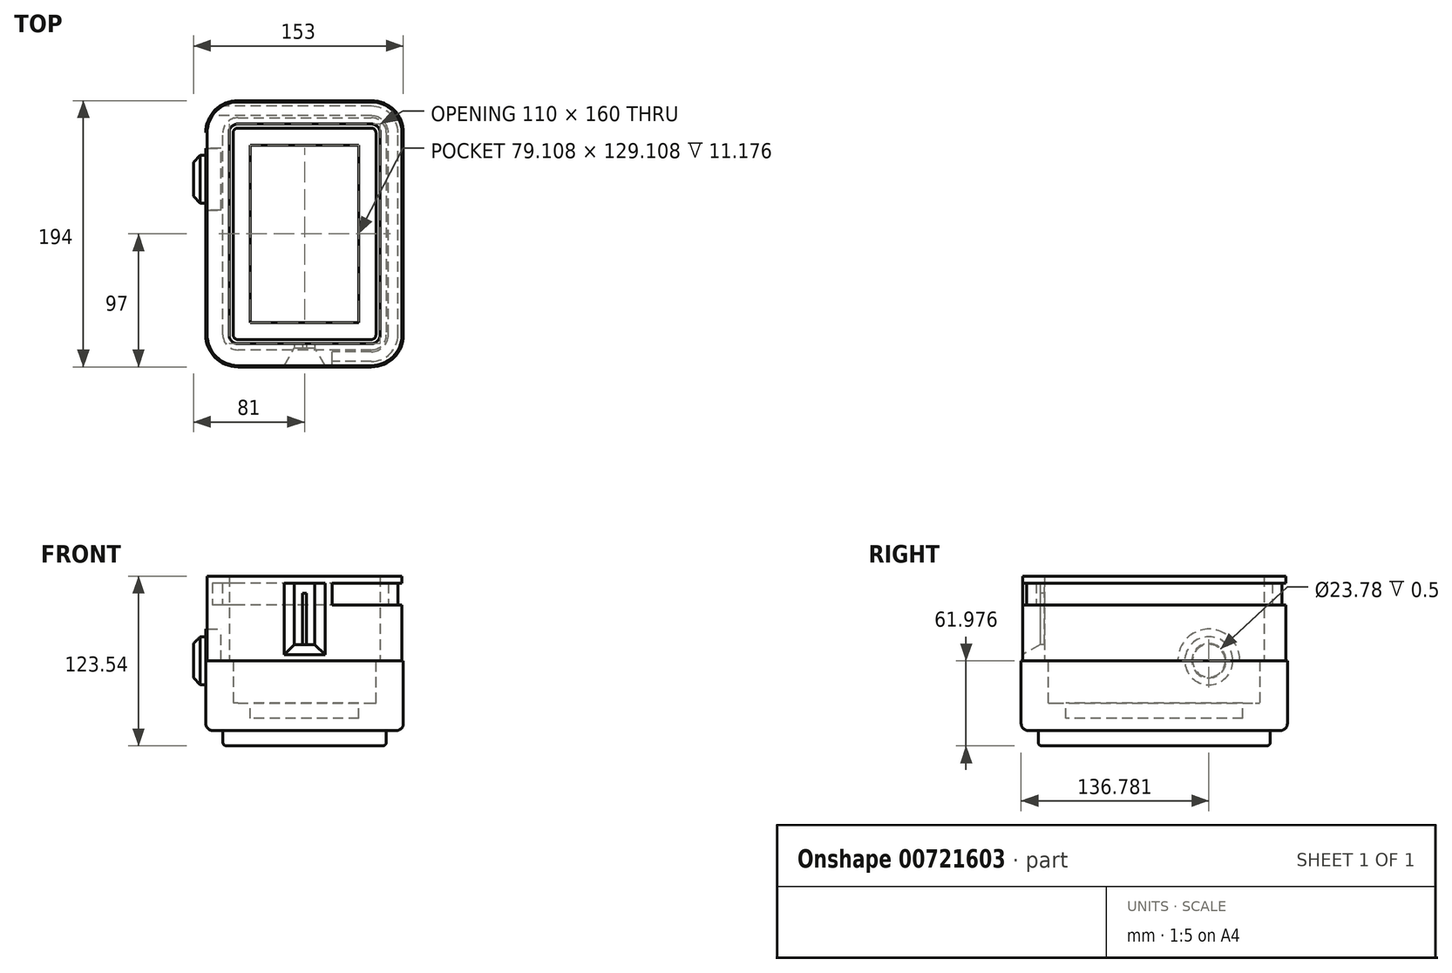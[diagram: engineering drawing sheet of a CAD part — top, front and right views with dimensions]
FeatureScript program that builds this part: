
annotation { "Feature Type Name" : "Feature", "Feature Type Description" : "" }
export const myFeature = defineFeature(function(context is Context, id is Id, definition is map)
    precondition{}
    {
        {
            var Q0;
            Q0=qCreatedBy(makeId("Top.planeOp"),FACE);
            var sketch = newSketch(context, id + "F0", { "sketchPlane" : qUnion([Q0])});
            skLineSegment(sketch, "E0.bottom", {"start": v(-21.35, -6.35) * mm, "end": v(-118.65, -6.35) * mm});
            skLineSegment(sketch, "E0.top", {"start": v(-21.35, 153.65) * mm, "end": v(-118.65, 153.65) * mm});
            skLineSegment(sketch, "E0.left", {"start": v(-15, 0) * mm, "end": v(-15, 147.3) * mm});
            skLineSegment(sketch, "E0.right", {"start": v(-125, 0) * mm, "end": v(-125, 147.3) * mm});
            skPoint(sketch, "E1.visualSharp", {"position": v(-125, 153.65) * mm});
            skArc(sketch, "E1.filletArc", {"start": v(-118.65, 153.65) * mm, "mid": v(-123.14, 151.8) * mm, "end": v(-125, 147.3) * mm});
            skPoint(sketch, "E2.visualSharp", {"position": v(-15, 153.65) * mm});
            skArc(sketch, "E2.filletArc", {"start": v(-15, 147.3) * mm, "mid": v(-16.86, 151.8) * mm, "end": v(-21.35, 153.65) * mm});
            skPoint(sketch, "E3.visualSharp", {"position": v(-15, -6.35) * mm});
            skArc(sketch, "E3.filletArc", {"start": v(-21.35, -6.35) * mm, "mid": v(-16.86, -4.5) * mm, "end": v(-15, 0) * mm});
            skPoint(sketch, "E4.visualSharp", {"position": v(-125, -6.35) * mm});
            skArc(sketch, "E4.filletArc", {"start": v(-125, 0) * mm, "mid": v(-123.14, -4.5) * mm, "end": v(-118.65, -6.35) * mm});
            skArc(sketch, "E5.0", {"start": v(-140, 0) * mm, "mid": v(-133.75, -15.1) * mm, "end": v(-118.65, -21.35) * mm});
            skLineSegment(sketch, "E5.1", {"start": v(-21.35, -21.35) * mm, "end": v(-118.65, -21.35) * mm});
            skLineSegment(sketch, "E5.2", {"start": v(-140, 0) * mm, "end": v(-140, 147.3) * mm});
            skArc(sketch, "E5.3", {"start": v(-21.35, -21.35) * mm, "mid": v(-6.25, -15.1) * mm, "end": v(0, 0) * mm});
            skArc(sketch, "E5.4", {"start": v(-118.65, 168.65) * mm, "mid": v(-133.75, 162.4) * mm, "end": v(-140, 147.3) * mm});
            skLineSegment(sketch, "E5.5", {"start": v(-21.35, 168.65) * mm, "end": v(-118.65, 168.65) * mm});
            skArc(sketch, "E5.6", {"start": v(0, 147.3) * mm, "mid": v(-6.25, 162.4) * mm, "end": v(-21.35, 168.65) * mm});
            skLineSegment(sketch, "E5.7", {"start": v(0, 0) * mm, "end": v(0, 147.3) * mm});
            skPoint(sketch, "E6.visualSharp", {"position": v(-322.23, 56.74) * mm});
            skPoint(sketch, "E7.visualSharp", {"position": v(-212.23, 56.74) * mm});
            skPoint(sketch, "E8.visualSharp", {"position": v(-212.23, -103.26) * mm});
            skPoint(sketch, "E9.visualSharp", {"position": v(-322.23, -103.26) * mm});
            skLineSegment(sketch, "E10.0", {"start": v(-21.35, 169.65) * mm, "end": v(-118.65, 169.65) * mm});
            skArc(sketch, "E10.1", {"start": v(1, 147.3) * mm, "mid": v(-5.55, 163.1) * mm, "end": v(-21.35, 169.65) * mm});
            skArc(sketch, "E10.2", {"start": v(-118.65, 169.65) * mm, "mid": v(-134.45, 163.1) * mm, "end": v(-141, 147.3) * mm});
            skLineSegment(sketch, "E10.3", {"start": v(1, 0) * mm, "end": v(1, 147.3) * mm});
            skLineSegment(sketch, "E10.4", {"start": v(-141, 0) * mm, "end": v(-141, 147.3) * mm});
            skArc(sketch, "E10.5", {"start": v(-141, 0) * mm, "mid": v(-134.45, -15.8) * mm, "end": v(-118.65, -22.35) * mm});
            skLineSegment(sketch, "E10.6", {"start": v(-21.35, -22.35) * mm, "end": v(-118.65, -22.35) * mm});
            skArc(sketch, "E10.7", {"start": v(-21.35, -22.35) * mm, "mid": v(-5.55, -15.8) * mm, "end": v(1, 0) * mm});
            skSolve(sketch);
        }
        {
            var Q0;
            Q0=makeQuery(id+"F0.imprint","IMPRINT",FACE,{"disambiguationData":[TD([[makeQuery(id+"F0.imprint","IMPRINT",EDGE,{"derivedFrom":sQuery(id+"F0.wireOp",EDGE,"E0.bottom")}),1.0]])]});
            var Q1;
            Q1=makeQuery(id+"F0.imprint","IMPRINT",FACE,{"disambiguationData":[TD([[makeQuery(id+"F0.imprint","IMPRINT",EDGE,{"derivedFrom":sQuery(id+"F0.wireOp",EDGE,"E5.0")}),-1.0]])]});
            extrude(context, id + "F1", {"entities" : qUnion([Q0, Q1]), "depth" : 100 * mm, "offsetDistance" : 25.4 * mm});
        }
        {
            var Q0;
            Q0=makeQuery(id+"F1.opExtrude","CAP_FACE",FACE,{"disambiguationData":[OSD([sQuery(id+"F0.wireOp",EDGE,"E0.bottom"),sQuery(id+"F0.wireOp",EDGE,"E0.top"),sQuery(id+"F0.wireOp",EDGE,"E0.left"),sQuery(id+"F0.wireOp",EDGE,"E0.right"),sQuery(id+"F0.wireOp",EDGE,"E1.filletArc"),sQuery(id+"F0.wireOp",EDGE,"E2.filletArc"),sQuery(id+"F0.wireOp",EDGE,"E3.filletArc"),sQuery(id+"F0.wireOp",EDGE,"E4.filletArc"),sQuery(id+"F0.wireOp",EDGE,"E10.0"),sQuery(id+"F0.wireOp",EDGE,"E10.1"),sQuery(id+"F0.wireOp",EDGE,"E10.2"),sQuery(id+"F0.wireOp",EDGE,"E10.3"),sQuery(id+"F0.wireOp",EDGE,"E10.4"),sQuery(id+"F0.wireOp",EDGE,"E10.5"),sQuery(id+"F0.wireOp",EDGE,"E10.6"),sQuery(id+"F0.wireOp",EDGE,"E10.7")])],"isStart":false});
            var sketch = newSketch(context, id + "F2", { "sketchPlane" : qUnion([Q0])});
            skArc(sketch, "E11.0", {"start": v(-9, 147.3) * mm, "mid": v(-12.62, 156.03) * mm, "end": v(-21.35, 159.65) * mm});
            skLineSegment(sketch, "E11.1", {"start": v(-9, 0) * mm, "end": v(-9, 147.3) * mm});
            skLineSegment(sketch, "E11.2", {"start": v(-21.35, 159.65) * mm, "end": v(-118.65, 159.65) * mm});
            skArc(sketch, "E11.3", {"start": v(-21.35, -12.35) * mm, "mid": v(-12.62, -8.73) * mm, "end": v(-9, 0) * mm});
            skArc(sketch, "E11.4", {"start": v(-118.65, 159.65) * mm, "mid": v(-127.38, 156.03) * mm, "end": v(-131, 147.3) * mm});
            skLineSegment(sketch, "E11.5", {"start": v(-131, 0) * mm, "end": v(-131, 147.3) * mm});
            skArc(sketch, "E11.6", {"start": v(-131, 0) * mm, "mid": v(-127.38, -8.73) * mm, "end": v(-118.65, -12.35) * mm});
            skLineSegment(sketch, "E11.7", {"start": v(-21.35, -12.35) * mm, "end": v(-118.65, -12.35) * mm});
            skLineSegment(sketch, "E12", {"start": v(-118.65, 159.65) * mm, "end": v(-137.28, 159.65) * mm});
            skLineSegment(sketch, "E13", {"start": v(-50, -22.35) * mm, "end": v(-50, -12.35) * mm});
            skPoint(sketch, "E14", {"position": v(-70, -12.35) * mm});
            skSolve(sketch);
        }
        {
            var Q0;
            Q0=makeQuery(id+"F2.imprint","IMPRINT",FACE,{"disambiguationData":[TD([[makeQuery(id+"F2.imprint","IMPRINT",EDGE,{"derivedFrom":sQuery(id+"F2.wireOp",EDGE,"E11.4")}),-1.0]])]});
            var Q1;
            Q1=makeQuery(id+"F2.imprint","IMPRINT",FACE,{"disambiguationData":[TD([[makeQuery(id+"F2.imprint","IMPRINT",EDGE,{"derivedFrom":sQuery(id+"F2.wireOp",EDGE,"E11.0")}),1.0]])]});
            extrude(context, id + "F3", {"entities" : qUnion([Q0, Q1]), "operationType" : NewBodyOperationType.ADD, "depth" : 16 * mm, "offsetDistance" : 25.4 * mm});
        }
        {
            var Q0;
            Q0=makeQuery(id+"F3.opExtrude","CAP_FACE",FACE,{"disambiguationData":[OSD([sQuery(id+"F0.wireOp",EDGE,"E0.bottom"),sQuery(id+"F0.wireOp",EDGE,"E0.top"),sQuery(id+"F0.wireOp",EDGE,"E0.left"),sQuery(id+"F0.wireOp",EDGE,"E0.right"),sQuery(id+"F0.wireOp",EDGE,"E1.filletArc"),sQuery(id+"F0.wireOp",EDGE,"E2.filletArc"),sQuery(id+"F0.wireOp",EDGE,"E3.filletArc"),sQuery(id+"F0.wireOp",EDGE,"E4.filletArc"),sQuery(id+"F0.wireOp",EDGE,"E10.2"),sQuery(id+"F0.wireOp",EDGE,"E10.4"),sQuery(id+"F0.wireOp",EDGE,"E10.5"),sQuery(id+"F0.wireOp",EDGE,"E10.6"),sQuery(id+"F2.wireOp",EDGE,"E11.0"),sQuery(id+"F2.wireOp",EDGE,"E11.1"),sQuery(id+"F2.wireOp",EDGE,"E11.2"),sQuery(id+"F2.wireOp",EDGE,"E11.3"),sQuery(id+"F2.wireOp",EDGE,"E11.7"),sQuery(id+"F2.wireOp",EDGE,"E12"),sQuery(id+"F2.wireOp",EDGE,"E13")])],"isStart":false});
            var sketch = newSketch(context, id + "F4", { "sketchPlane" : qUnion([Q0])});
            skSolve(sketch);
        }
        {
            var Q0;
            Q0=makeQuery(id+"F4.imprint","IMPRINT",FACE,{"disambiguationData":[TD([[makeQuery(id+"F4.imprint","IMPRINT",EDGE,{"derivedFrom":makeQuery(id+"F3.opExtrude","CAP_EDGE",EDGE,{"disambiguationData":[OSD([sQuery(id+"F2.wireOp",EDGE,"E11.0")])],"isStart":false})}),1.0]])]});
            var sketch = newSketch(context, id + "F5", { "sketchPlane" : qUnion([Q0])});
            skArc(sketch, "E15.0", {"start": v(-141, 0) * mm, "mid": v(-134.45, -15.8) * mm, "end": v(-118.65, -22.35) * mm});
            skLineSegment(sketch, "E15.1", {"start": v(-21.35, -22.35) * mm, "end": v(-118.65, -22.35) * mm});
            skLineSegment(sketch, "E15.2", {"start": v(-141, 0) * mm, "end": v(-141, 147.3) * mm});
            skArc(sketch, "E15.3", {"start": v(-21.35, -22.35) * mm, "mid": v(-5.55, -15.8) * mm, "end": v(1, 0) * mm});
            skArc(sketch, "E15.4", {"start": v(-118.65, 169.65) * mm, "mid": v(-134.45, 163.1) * mm, "end": v(-141, 147.3) * mm});
            skLineSegment(sketch, "E15.5", {"start": v(-21.35, 169.65) * mm, "end": v(-118.65, 169.65) * mm});
            skArc(sketch, "E15.6", {"start": v(1, 147.3) * mm, "mid": v(-5.55, 163.1) * mm, "end": v(-21.35, 169.65) * mm});
            skLineSegment(sketch, "E15.7", {"start": v(1, 0) * mm, "end": v(1, 147.3) * mm});
            skSolve(sketch);
        }
        {
            var Q0;
            Q0=makeQuery(id+"F4.imprint","IMPRINT",FACE,{"disambiguationData":[TD([[makeQuery(id+"F4.imprint","IMPRINT",EDGE,{"derivedFrom":makeQuery(id+"F3.opExtrude","CAP_EDGE",EDGE,{"disambiguationData":[OSD([sQuery(id+"F2.wireOp",EDGE,"E11.0")])],"isStart":false})}),1.0]])]});
            var Q1;
            {var subQ3=sQuery(id+"F5.wireOp",EDGE,"E15.3");Q1=makeQuery(id+"F5.imprint","IMPRINT",FACE,{"disambiguationData":[TD([[makeQuery(id+"F5.imprint","IMPRINT",EDGE,{"derivedFrom":subQ3}),1.0]])]});}
            extrude(context, id + "F6", {"entities" : qUnion([Q0, Q1]), "operationType" : NewBodyOperationType.ADD, "depth" : 5 * mm, "offsetDistance" : 25.4 * mm});
        }
        {
            var Q0;
            Q0=makeQuery(id+"F1.opExtrude","CAP_FACE",FACE,{"disambiguationData":[OSD([sQuery(id+"F0.wireOp",EDGE,"E0.bottom"),sQuery(id+"F0.wireOp",EDGE,"E0.top"),sQuery(id+"F0.wireOp",EDGE,"E0.left"),sQuery(id+"F0.wireOp",EDGE,"E0.right"),sQuery(id+"F0.wireOp",EDGE,"E1.filletArc"),sQuery(id+"F0.wireOp",EDGE,"E2.filletArc"),sQuery(id+"F0.wireOp",EDGE,"E3.filletArc"),sQuery(id+"F0.wireOp",EDGE,"E4.filletArc"),sQuery(id+"F0.wireOp",EDGE,"E10.0"),sQuery(id+"F0.wireOp",EDGE,"E10.1"),sQuery(id+"F0.wireOp",EDGE,"E10.2"),sQuery(id+"F0.wireOp",EDGE,"E10.3"),sQuery(id+"F0.wireOp",EDGE,"E10.4"),sQuery(id+"F0.wireOp",EDGE,"E10.5"),sQuery(id+"F0.wireOp",EDGE,"E10.6"),sQuery(id+"F0.wireOp",EDGE,"E10.7")])],"isStart":false});
            var sketch = newSketch(context, id + "F7", { "sketchPlane" : qUnion([Q0])});
            skLineSegment(sketch, "E16.0", {"start": v(-21.35, -19.35) * mm, "end": v(-50, -19.35) * mm});
            skLineSegment(sketch, "E16.1", {"start": v(-21.35, 166.65) * mm, "end": v(-137.28, 166.65) * mm});
            skArc(sketch, "E16.2", {"start": v(-2, 147.3) * mm, "mid": v(-7.67, 160.98) * mm, "end": v(-21.35, 166.65) * mm});
            skLineSegment(sketch, "E16.3", {"start": v(-2, 0) * mm, "end": v(-2, 147.3) * mm});
            skArc(sketch, "E16.4", {"start": v(-21.35, -19.35) * mm, "mid": v(-7.67, -13.68) * mm, "end": v(-2, 0) * mm});
            skLineSegment(sketch, "E17", {"start": v(-137.28, 159.65) * mm, "end": v(-137.28, 166.65) * mm});
            skLineSegment(sketch, "E18", {"start": v(-50, -19.35) * mm, "end": v(-50, -12.35) * mm});
            skSolve(sketch);
        }
        {
            var Q0;
            Q0=makeQuery(id+"F7.imprint","IMPRINT",FACE,{"disambiguationData":[TD([[makeQuery(id+"F7.imprint","IMPRINT",EDGE,{"derivedFrom":sQuery(id+"F7.wireOp",EDGE,"E16.0")}),-1.0]])]});
            extrude(context, id + "F8", {"entities" : qUnion([Q0]), "endBound" : BoundingType.UP_TO_NEXT, "depth" : 8.38 * mm, "offsetDistance" : 25.4 * mm});
        }
        {
            var Q0;
            {var subQ0=sQuery(id+"F0.wireOp",EDGE,"E10.4");Q0=makeQuery(id+"F6.boolean.opBoolean","MERGE",FACE,{"derivedFrom":[makeQuery(id+"F3.boolean.opBoolean","MERGE",FACE,{"derivedFrom":[makeQuery(id+"F1.opExtrude","SWEPT_FACE",FACE,{"disambiguationData":[OSD([subQ0])]}),makeQuery(id+"F3.opExtrude","SWEPT_FACE",FACE,{"disambiguationData":[OSD([subQ0])]})]}),makeQuery(id+"F6.opExtrude","SWEPT_FACE",FACE,{"disambiguationData":[OSD([subQ0])]})]});}
            var sketch = newSketch(context, id + "F9", { "sketchPlane" : qUnion([Q0])});
            skCircle(sketch, "E19", {"center": v(-113.43, 60) * mm, "radius": 22.5 * mm});
            skSolve(sketch);
        }
        {
            var Q0;
            Q0=makeQuery(id+"F9.imprint","IMPRINT",FACE,{"disambiguationData":[TD([[makeQuery(id+"F9.imprint","IMPRINT",EDGE,{"derivedFrom":sQuery(id+"F9.wireOp",EDGE,"E19")}),1.0]])]});
            extrude(context, id + "F10", {"entities" : qUnion([Q0]), "operationType" : NewBodyOperationType.REMOVE, "oppositeDirection" : true, "depth" : 10 * mm, "offsetDistance" : 25.4 * mm});
        }
        {
            var Q0;
            Q0=makeQuery(id+"F1.opExtrude","CAP_FACE",FACE,{"disambiguationData":[OSD([sQuery(id+"F0.wireOp",EDGE,"E0.bottom"),sQuery(id+"F0.wireOp",EDGE,"E0.top"),sQuery(id+"F0.wireOp",EDGE,"E0.left"),sQuery(id+"F0.wireOp",EDGE,"E0.right"),sQuery(id+"F0.wireOp",EDGE,"E1.filletArc"),sQuery(id+"F0.wireOp",EDGE,"E2.filletArc"),sQuery(id+"F0.wireOp",EDGE,"E3.filletArc"),sQuery(id+"F0.wireOp",EDGE,"E4.filletArc"),sQuery(id+"F0.wireOp",EDGE,"E10.0"),sQuery(id+"F0.wireOp",EDGE,"E10.1"),sQuery(id+"F0.wireOp",EDGE,"E10.2"),sQuery(id+"F0.wireOp",EDGE,"E10.3"),sQuery(id+"F0.wireOp",EDGE,"E10.4"),sQuery(id+"F0.wireOp",EDGE,"E10.5"),sQuery(id+"F0.wireOp",EDGE,"E10.6"),sQuery(id+"F0.wireOp",EDGE,"E10.7")])],"isStart":true});
            extrude(context, id + "F11", {"entities" : qUnion([Q0]), "operationType" : NewBodyOperationType.REMOVE, "oppositeDirection" : true, "depth" : 59.44 * mm, "offsetDistance" : 25.4 * mm});
        }
        {
            var Q0;
            Q0=makeQuery(id+"F10.boolean.opBoolean","COPY",FACE,{"derivedFrom":makeQuery(id+"F10.opExtrude","CAP_FACE",FACE,{"disambiguationData":[OSD([sQuery(id+"F9.wireOp",EDGE,"E19")])],"isStart":false})});
            extrude(context, id + "F12", {"entities" : qUnion([Q0]), "depth" : 11 * mm, "offsetDistance" : 25.4 * mm});
        }
        {
            var Q0;
            Q0=makeQuery(id+"F12.opExtrude","SWEPT_FACE",FACE,{"disambiguationData":[OSD([sQuery(id+"F0.wireOp",EDGE,"E0.bottom"),sQuery(id+"F0.wireOp",EDGE,"E0.top"),sQuery(id+"F0.wireOp",EDGE,"E0.left"),sQuery(id+"F0.wireOp",EDGE,"E0.right"),sQuery(id+"F0.wireOp",EDGE,"E1.filletArc"),sQuery(id+"F0.wireOp",EDGE,"E2.filletArc"),sQuery(id+"F0.wireOp",EDGE,"E3.filletArc"),sQuery(id+"F0.wireOp",EDGE,"E4.filletArc"),sQuery(id+"F0.wireOp",EDGE,"E10.0"),sQuery(id+"F0.wireOp",EDGE,"E10.1"),sQuery(id+"F0.wireOp",EDGE,"E10.2"),sQuery(id+"F0.wireOp",EDGE,"E10.3"),sQuery(id+"F0.wireOp",EDGE,"E10.4"),sQuery(id+"F0.wireOp",EDGE,"E10.5"),sQuery(id+"F0.wireOp",EDGE,"E10.6"),sQuery(id+"F0.wireOp",EDGE,"E10.7"),sQuery(id+"F9.wireOp",EDGE,"E19")])]});
            var sketch = newSketch(context, id + "F13", { "sketchPlane" : qUnion([Q0])});
            skPoint(sketch, "E20", {"position": v(-142, -135.92) * mm});
            skLineSegment(sketch, "E21", {"start": v(-142, -135.92) * mm, "end": v(-142, -90.94) * mm});
            skLineSegment(sketch, "E22.0", {"start": v(-142, -134.92) * mm, "end": v(-132, -134.92) * mm});
            skLineSegment(sketch, "E22.1", {"start": v(2, -147.3) * mm, "end": v(2, 0) * mm});
            skArc(sketch, "E22.2", {"start": v(-21.35, -170.65) * mm, "mid": v(-4.84, -163.81) * mm, "end": v(2, -147.3) * mm});
            skLineSegment(sketch, "E22.3", {"start": v(-118.65, -170.65) * mm, "end": v(-21.35, -170.65) * mm});
            skArc(sketch, "E22.4", {"start": v(-142, -147.3) * mm, "mid": v(-135.16, -163.81) * mm, "end": v(-118.65, -170.65) * mm});
            skArc(sketch, "E22.5", {"start": v(2, 0) * mm, "mid": v(-4.84, 16.51) * mm, "end": v(-21.35, 23.35) * mm});
            skLineSegment(sketch, "E22.6", {"start": v(-142, -134.92) * mm, "end": v(-142, -147.3) * mm});
            skLineSegment(sketch, "E22.7", {"start": v(-21.35, 23.35) * mm, "end": v(-118.65, 23.35) * mm});
            skArc(sketch, "E22.8", {"start": v(-118.65, 23.35) * mm, "mid": v(-135.16, 16.51) * mm, "end": v(-142, 0) * mm});
            skLineSegment(sketch, "E22.9", {"start": v(-142, 0) * mm, "end": v(-142, -91.94) * mm});
            skLineSegment(sketch, "E22.10", {"start": v(-142, -91.94) * mm, "end": v(-132, -91.94) * mm});
            skLineSegment(sketch, "E22.11", {"start": v(-132, -91.94) * mm, "end": v(-132, -134.92) * mm});
            skLineSegment(sketch, "E23", {"start": v(-142, -90.94) * mm, "end": v(-142, -135.92) * mm});
            skSolve(sketch);
        }
        {
            var Q0;
            Q0=makeQuery(id+"F13.imprint","IMPRINT",FACE,{"disambiguationData":[TD([[makeQuery(id+"F13.imprint","IMPRINT",EDGE,{"derivedFrom":sQuery(id+"F13.wireOp",EDGE,"E22.1")}),1.0]])]});
            var Q1;
            {var subQ0=sQuery(id+"F13.wireOp",EDGE,"E22.0");Q1=makeQuery(id+"F13.imprint","IMPRINT",FACE,{"disambiguationData":[TD([[makeQuery(id+"F13.imprint","IMPRINT",EDGE,{"derivedFrom":subQ0}),1.0]])]});}
            var Q2;
            {var subQ23=sQuery(id+"F13.wireOp",EDGE,"E22.0");Q2=makeQuery(id+"F13.imprint","IMPRINT",FACE,{"disambiguationData":[TD([[makeQuery(id+"F13.imprint","IMPRINT",EDGE,{"derivedFrom":subQ23}),-1.0]])]});}
            extrude(context, id + "F14", {"entities" : qUnion([Q0, Q1, Q2]), "depth" : 50.8 * mm, "offsetDistance" : 25.4 * mm});
        }
        {
            var Q0;
            Q0=makeQuery(id+"F14.opExtrude","CAP_FACE",FACE,{"disambiguationData":[OSD([sQuery(id+"F13.wireOp",EDGE,"E22.1"),sQuery(id+"F13.wireOp",EDGE,"E22.2"),sQuery(id+"F13.wireOp",EDGE,"E22.3"),sQuery(id+"F13.wireOp",EDGE,"E22.4"),sQuery(id+"F13.wireOp",EDGE,"E22.5"),sQuery(id+"F13.wireOp",EDGE,"E22.6"),sQuery(id+"F13.wireOp",EDGE,"E22.7"),sQuery(id+"F13.wireOp",EDGE,"E22.8"),sQuery(id+"F13.wireOp",EDGE,"E22.9"),sQuery(id+"F13.wireOp",EDGE,"E23")])],"isStart":false});
            fillet(context, id + "F15", {"entities" : qUnion([Q0]), "radius" : 5.08 * mm, "tangentPropagation" : true, "allowEdgeOverflow" : false});
        }
        {
            var Q0;
            Q0=makeQuery(id+"F12.opExtrude","CAP_FACE",FACE,{"disambiguationData":[OSD([sQuery(id+"F9.wireOp",EDGE,"E19")])],"isStart":false});
            var sketch = newSketch(context, id + "F16", { "sketchPlane" : qUnion([Q0])});
            skPoint(sketch, "E24", {"position": v(-113.43, 59.44) * mm});
            skCircle(sketch, "E25", {"center": v(-113.43, 59.44) * mm, "radius": 17.5 * mm});
            skSolve(sketch);
        }
        {
            var Q0;
            {var subQ0=sQuery(id+"F16.wireOp",EDGE,"E25");var subQ1=makeQuery(id+"F12.opExtrude","CAP_EDGE",EDGE,{"disambiguationData":[OSD([sQuery(id+"F0.wireOp",EDGE,"E0.bottom"),sQuery(id+"F0.wireOp",EDGE,"E0.top"),sQuery(id+"F0.wireOp",EDGE,"E0.left"),sQuery(id+"F0.wireOp",EDGE,"E0.right"),sQuery(id+"F0.wireOp",EDGE,"E1.filletArc"),sQuery(id+"F0.wireOp",EDGE,"E2.filletArc"),sQuery(id+"F0.wireOp",EDGE,"E3.filletArc"),sQuery(id+"F0.wireOp",EDGE,"E4.filletArc"),sQuery(id+"F0.wireOp",EDGE,"E10.0"),sQuery(id+"F0.wireOp",EDGE,"E10.1"),sQuery(id+"F0.wireOp",EDGE,"E10.2"),sQuery(id+"F0.wireOp",EDGE,"E10.3"),sQuery(id+"F0.wireOp",EDGE,"E10.4"),sQuery(id+"F0.wireOp",EDGE,"E10.5"),sQuery(id+"F0.wireOp",EDGE,"E10.6"),sQuery(id+"F0.wireOp",EDGE,"E10.7"),sQuery(id+"F9.wireOp",EDGE,"E19")])],"isStart":false});var subQ2=makeQuery(id+"F16.imprint","INTERSECT",VERTEX,{"disambiguationData":[OD(0.0)],"derivedFrom":[subQ1,subQ0]});Q0=makeQuery(id+"F16.imprint","IMPRINT",FACE,{"disambiguationData":[TD([[makeQuery(id+"F16.imprint","IMPRINT",EDGE,{"disambiguationData":[TD([[subQ2,1.0]])],"derivedFrom":subQ0}),1.0]])]});}
            var Q1;
            {var subQ0=sQuery(id+"F16.wireOp",EDGE,"E25");var subQ1=makeQuery(id+"F12.opExtrude","CAP_EDGE",EDGE,{"disambiguationData":[OSD([sQuery(id+"F0.wireOp",EDGE,"E0.bottom"),sQuery(id+"F0.wireOp",EDGE,"E0.top"),sQuery(id+"F0.wireOp",EDGE,"E0.left"),sQuery(id+"F0.wireOp",EDGE,"E0.right"),sQuery(id+"F0.wireOp",EDGE,"E1.filletArc"),sQuery(id+"F0.wireOp",EDGE,"E2.filletArc"),sQuery(id+"F0.wireOp",EDGE,"E3.filletArc"),sQuery(id+"F0.wireOp",EDGE,"E4.filletArc"),sQuery(id+"F0.wireOp",EDGE,"E10.0"),sQuery(id+"F0.wireOp",EDGE,"E10.1"),sQuery(id+"F0.wireOp",EDGE,"E10.2"),sQuery(id+"F0.wireOp",EDGE,"E10.3"),sQuery(id+"F0.wireOp",EDGE,"E10.4"),sQuery(id+"F0.wireOp",EDGE,"E10.5"),sQuery(id+"F0.wireOp",EDGE,"E10.6"),sQuery(id+"F0.wireOp",EDGE,"E10.7"),sQuery(id+"F9.wireOp",EDGE,"E19")])],"isStart":false});var subQ2=makeQuery(id+"F16.imprint","INTERSECT",VERTEX,{"disambiguationData":[OD(0.0)],"derivedFrom":[subQ1,subQ0]});Q1=makeQuery(id+"F16.imprint","IMPRINT",FACE,{"disambiguationData":[TD([[makeQuery(id+"F16.imprint","IMPRINT",EDGE,{"disambiguationData":[TD([[subQ2,-1.0]])],"derivedFrom":subQ0}),1.0]])]});}
            extrude(context, id + "F17", {"entities" : qUnion([Q0, Q1]), "depth" : 9 * mm, "offsetDistance" : 25.4 * mm});
        }
        {
            var Q0;
            Q0=makeQuery(id+"F17.opExtrude","CAP_FACE",FACE,{"disambiguationData":[OSD([sQuery(id+"F16.wireOp",EDGE,"E25")])],"isStart":false});
            chamfer(context, id + "F18", {"entities" : qUnion([Q0]), "width" : 5 * mm, "tangentPropagation" : true});
        }
        {
            var Q0;
            Q0=makeQuery(id+"F17.opExtrude","CAP_FACE",FACE,{"disambiguationData":[OSD([sQuery(id+"F16.wireOp",EDGE,"E25")])],"isStart":false});
            var sketch = newSketch(context, id + "F19", { "sketchPlane" : qUnion([Q0])});
            skCircle(sketch, "E26", {"center": v(-113.43, 59.44) * mm, "radius": 11.89 * mm});
            skSolve(sketch);
        }
        {
            var Q0;
            Q0=makeQuery(id+"F19.imprint","IMPRINT",FACE,{"disambiguationData":[TD([[makeQuery(id+"F19.imprint","IMPRINT",EDGE,{"derivedFrom":sQuery(id+"F19.wireOp",EDGE,"E26")}),1.0]])]});
            extrude(context, id + "F20", {"entities" : qUnion([Q0]), "operationType" : NewBodyOperationType.REMOVE, "oppositeDirection" : true, "depth" : 1 * mm, "offsetDistance" : 25.4 * mm});
        }
        {
            var Q0;
            Q0=makeQuery(id+"F20.boolean.opBoolean","COPY",FACE,{"derivedFrom":makeQuery(id+"F20.opExtrude","CAP_FACE",FACE,{"disambiguationData":[OSD([sQuery(id+"F19.wireOp",EDGE,"E26")])],"isStart":false})});
            extrude(context, id + "F21", {"entities" : qUnion([Q0]), "operationType" : NewBodyOperationType.ADD, "depth" : 0.5 * mm, "offsetDistance" : 25.4 * mm});
        }
        {
            var Q0;
            Q0=makeQuery(id+"F21.opExtrude","CAP_FACE",FACE,{"disambiguationData":[OSD([sQuery(id+"F19.wireOp",EDGE,"E26")])],"isStart":false});
            extrude(context, id + "F22", {"entities" : qUnion([Q0]), "depth" : 0.5 * mm, "offsetDistance" : 25.4 * mm});
        }
        {
            var Q0;
            Q0=makeQuery(id+"F14.opExtrude","CAP_FACE",FACE,{"disambiguationData":[OSD([sQuery(id+"F13.wireOp",EDGE,"E22.1"),sQuery(id+"F13.wireOp",EDGE,"E22.2"),sQuery(id+"F13.wireOp",EDGE,"E22.3"),sQuery(id+"F13.wireOp",EDGE,"E22.4"),sQuery(id+"F13.wireOp",EDGE,"E22.5"),sQuery(id+"F13.wireOp",EDGE,"E22.6"),sQuery(id+"F13.wireOp",EDGE,"E22.7"),sQuery(id+"F13.wireOp",EDGE,"E22.8"),sQuery(id+"F13.wireOp",EDGE,"E22.9"),sQuery(id+"F13.wireOp",EDGE,"E23")])],"isStart":false});
            var sketch = newSketch(context, id + "F23", { "sketchPlane" : qUnion([Q0])});
            skArc(sketch, "E27.0", {"start": v(-21.35, -158.2) * mm, "mid": v(-13.64, -155.01) * mm, "end": v(-10.45, -147.3) * mm});
            skLineSegment(sketch, "E27.1", {"start": v(-118.65, -158.2) * mm, "end": v(-21.35, -158.2) * mm});
            skLineSegment(sketch, "E27.2", {"start": v(-10.45, -147.3) * mm, "end": v(-10.45, 0) * mm});
            skArc(sketch, "E27.3", {"start": v(-129.55, -147.3) * mm, "mid": v(-126.36, -155.01) * mm, "end": v(-118.65, -158.2) * mm});
            skArc(sketch, "E27.4", {"start": v(-10.45, 0) * mm, "mid": v(-13.64, 7.71) * mm, "end": v(-21.35, 10.9) * mm});
            skLineSegment(sketch, "E27.5", {"start": v(-21.35, 10.9) * mm, "end": v(-118.65, 10.9) * mm});
            skArc(sketch, "E27.6", {"start": v(-118.65, 10.9) * mm, "mid": v(-126.36, 7.71) * mm, "end": v(-129.55, 0) * mm});
            skLineSegment(sketch, "E27.7", {"start": v(-129.55, 0) * mm, "end": v(-129.55, -147.3) * mm});
            skSolve(sketch);
        }
        {
            var Q0;
            Q0=makeQuery(id+"F23.imprint","IMPRINT",FACE,{"disambiguationData":[TD([[makeQuery(id+"F23.imprint","IMPRINT",EDGE,{"derivedFrom":sQuery(id+"F23.wireOp",EDGE,"E27.0")}),1.0]])]});
            extrude(context, id + "F24", {"entities" : qUnion([Q0]), "operationType" : NewBodyOperationType.ADD, "depth" : 11.18 * mm, "offsetDistance" : 25.4 * mm});
        }
        {
            var Q0;
            Q0=makeQuery(id+"F24.opExtrude","CAP_FACE",FACE,{"disambiguationData":[OSD([sQuery(id+"F23.wireOp",EDGE,"E27.0"),sQuery(id+"F23.wireOp",EDGE,"E27.1"),sQuery(id+"F23.wireOp",EDGE,"E27.2"),sQuery(id+"F23.wireOp",EDGE,"E27.3"),sQuery(id+"F23.wireOp",EDGE,"E27.4"),sQuery(id+"F23.wireOp",EDGE,"E27.5"),sQuery(id+"F23.wireOp",EDGE,"E27.6"),sQuery(id+"F23.wireOp",EDGE,"E27.7")])],"isStart":false});
            fillet(context, id + "F25", {"entities" : qUnion([Q0]), "radius" : 2.54 * mm, "tangentPropagation" : true, "allowEdgeOverflow" : false});
        }
        {
            var Q0;
            {var subQ0=sQuery(id+"F2.wireOp",EDGE,"E13");var subQ1=sQuery(id+"F2.wireOp",EDGE,"E12");var subQ2=sQuery(id+"F2.wireOp",EDGE,"E11.7");var subQ3=sQuery(id+"F2.wireOp",EDGE,"E11.3");var subQ4=sQuery(id+"F2.wireOp",EDGE,"E11.2");var subQ5=sQuery(id+"F2.wireOp",EDGE,"E11.1");var subQ6=sQuery(id+"F2.wireOp",EDGE,"E11.0");Q0=makeQuery(id+"F6.boolean.opBoolean","MERGE",FACE,{"derivedFrom":[makeQuery(id+"F6.opExtrude","CAP_FACE",FACE,{"disambiguationData":[OSD([sQuery(id+"F0.wireOp",EDGE,"E0.bottom"),sQuery(id+"F0.wireOp",EDGE,"E0.top"),sQuery(id+"F0.wireOp",EDGE,"E0.left"),sQuery(id+"F0.wireOp",EDGE,"E0.right"),sQuery(id+"F0.wireOp",EDGE,"E1.filletArc"),sQuery(id+"F0.wireOp",EDGE,"E2.filletArc"),sQuery(id+"F0.wireOp",EDGE,"E3.filletArc"),sQuery(id+"F0.wireOp",EDGE,"E4.filletArc"),sQuery(id+"F0.wireOp",EDGE,"E10.2"),sQuery(id+"F0.wireOp",EDGE,"E10.4"),sQuery(id+"F0.wireOp",EDGE,"E10.5"),sQuery(id+"F0.wireOp",EDGE,"E10.6"),subQ6,subQ5,subQ4,subQ3,subQ2,subQ1,subQ0])],"isStart":false}),makeQuery(id+"F6.opExtrude","CAP_FACE",FACE,{"disambiguationData":[OSD([subQ6,subQ5,subQ4,subQ3,subQ2,subQ1,subQ0,sQuery(id+"F5.wireOp",EDGE,"E15.1"),sQuery(id+"F5.wireOp",EDGE,"E15.3"),sQuery(id+"F5.wireOp",EDGE,"E15.4"),sQuery(id+"F5.wireOp",EDGE,"E15.5"),sQuery(id+"F5.wireOp",EDGE,"E15.6"),sQuery(id+"F5.wireOp",EDGE,"E15.7")])],"isStart":false})]});}
            var sketch = newSketch(context, id + "F26", { "sketchPlane" : qUnion([Q0])});
            skPoint(sketch, "E28", {"position": v(-70, -6.35) * mm});
            skLineSegment(sketch, "E29.bottom", {"start": v(-85, -6.35) * mm, "end": v(-55, -6.35) * mm});
            skLineSegment(sketch, "E29.top", {"start": v(-85, -22.35) * mm, "end": v(-55, -22.35) * mm});
            skLineSegment(sketch, "E29.left", {"start": v(-85, -6.35) * mm, "end": v(-85, -22.35) * mm});
            skLineSegment(sketch, "E29.right", {"start": v(-55, -6.35) * mm, "end": v(-55, -22.35) * mm});
            skLineSegment(sketch, "E30", {"start": v(-85, -9.6) * mm, "end": v(-55, -9.6) * mm});
            skSolve(sketch);
        }
        {
            var Q0;
            {var subQ0=sQuery(id+"F26.wireOp",EDGE,"E29.top");Q0=makeQuery(id+"F26.imprint","IMPRINT",FACE,{"disambiguationData":[TD([[makeQuery(id+"F26.imprint","IMPRINT",EDGE,{"derivedFrom":subQ0}),-1.0]])]});}
            extrude(context, id + "F27", {"entities" : qUnion([Q0]), "operationType" : NewBodyOperationType.REMOVE, "oppositeDirection" : true, "depth" : 57.4 * mm, "offsetDistance" : 25.4 * mm});
        }
        {
            var Q0;
            Q0=makeQuery(id+"F27.boolean.opBoolean","COPY",FACE,{"derivedFrom":makeQuery(id+"F27.opExtrude","SWEPT_FACE",FACE,{"disambiguationData":[OSD([sQuery(id+"F26.wireOp",EDGE,"E29.left")])]})});
            var sketch = newSketch(context, id + "F28", { "sketchPlane" : qUnion([Q0])});
            skLineSegment(sketch, "E31.bottom", {"start": v(-9.6, 121) * mm, "end": v(-22.35, 121) * mm});
            skLineSegment(sketch, "E31.top", {"start": v(-9.6, 116) * mm, "end": v(-22.35, 116) * mm});
            skLineSegment(sketch, "E31.left", {"start": v(-9.6, 121) * mm, "end": v(-9.6, 116) * mm});
            skLineSegment(sketch, "E31.right", {"start": v(-22.35, 121) * mm, "end": v(-22.35, 116) * mm});
            skSolve(sketch);
        }
        {
            var Q0;
            Q0=makeQuery(id+"F28.imprint","IMPRINT",FACE,{"disambiguationData":[TD([[makeQuery(id+"F28.imprint","IMPRINT",EDGE,{"derivedFrom":sQuery(id+"F28.wireOp",EDGE,"E31.bottom")}),1.0]])]});
            extrude(context, id + "F29", {"entities" : qUnion([Q0]), "operationType" : NewBodyOperationType.ADD, "endBound" : BoundingType.UP_TO_NEXT, "depth" : 25.4 * mm, "offsetDistance" : 25.4 * mm});
        }
        {
            var Q0;
            Q0=makeQuery(id+"F27.boolean.opBoolean","COPY",EDGE,{"derivedFrom":makeQuery(id+"F27.opExtrude","SWEPT_EDGE",EDGE,{"disambiguationData":[OSD([sQuery(id+"F26.wireOp",EDGE,"E29.left"),sQuery(id+"F26.wireOp",EDGE,"E30")])]})});
            var Q1;
            Q1=makeQuery(id+"F27.boolean.opBoolean","COPY",EDGE,{"derivedFrom":makeQuery(id+"F27.opExtrude","CAP_EDGE",EDGE,{"disambiguationData":[OSD([sQuery(id+"F26.wireOp",EDGE,"E30")])],"isStart":false})});
            var Q2;
            Q2=makeQuery(id+"F27.boolean.opBoolean","COPY",EDGE,{"derivedFrom":makeQuery(id+"F27.opExtrude","SWEPT_EDGE",EDGE,{"disambiguationData":[OSD([sQuery(id+"F26.wireOp",EDGE,"E29.right"),sQuery(id+"F26.wireOp",EDGE,"E30")])]})});
            var Q3;
            Q3=makeQuery(id+"F29.opExtrude","SWEPT_EDGE",EDGE,{"disambiguationData":[OSD([sQuery(id+"F26.wireOp",EDGE,"E29.left"),sQuery(id+"F26.wireOp",EDGE,"E30"),sQuery(id+"F28.wireOp",EDGE,"E31.top"),sQuery(id+"F28.wireOp",EDGE,"E31.left")])]});
            chamfer(context, id + "F30", {"entities" : qUnion([Q0, Q1, Q2, Q3]), "chamferType" : ChamferType.OFFSET_ANGLE, "width" : 13 * mm, "oppositeDirection" : false, "angle" : 30 * degree});
        }
        {
            var Q0;
            Q0=makeQuery(id+"F27.boolean.opBoolean","COPY",FACE,{"derivedFrom":makeQuery(id+"F27.opExtrude","SWEPT_FACE",FACE,{"disambiguationData":[OSD([sQuery(id+"F26.wireOp",EDGE,"E30")])]})});
            var sketch = newSketch(context, id + "F31", { "sketchPlane" : qUnion([Q0])});
            skPoint(sketch, "E32", {"position": v(-70, 108.5) * mm});
            skPoint(sketch, "E33", {"position": v(-62.5, 89.8) * mm});
            skPoint(sketch, "E34", {"position": v(-70, 89.8) * mm});
            skLineSegment(sketch, "E35.bottom", {"start": v(-71.5, 108.5) * mm, "end": v(-68.5, 108.5) * mm});
            skLineSegment(sketch, "E35.top", {"start": v(-71.5, 71.1) * mm, "end": v(-68.5, 71.1) * mm});
            skLineSegment(sketch, "E35.left", {"start": v(-71.5, 108.5) * mm, "end": v(-71.5, 71.1) * mm});
            skLineSegment(sketch, "E35.right", {"start": v(-68.5, 108.5) * mm, "end": v(-68.5, 71.1) * mm});
            skSolve(sketch);
        }
        {
            var Q0;
            Q0=makeQuery(id+"F31.imprint","IMPRINT",FACE,{"disambiguationData":[TD([[makeQuery(id+"F31.imprint","IMPRINT",EDGE,{"derivedFrom":sQuery(id+"F31.wireOp",EDGE,"E35.bottom")}),1.0]])]});
            extrude(context, id + "F32", {"entities" : qUnion([Q0]), "operationType" : NewBodyOperationType.REMOVE, "oppositeDirection" : true, "depth" : 22.35 * mm, "offsetDistance" : 25.4 * mm});
        }
        {
            var Q0;
            Q0=makeQuery(id+"F14.opExtrude","CAP_FACE",FACE,{"disambiguationData":[OSD([sQuery(id+"F13.wireOp",EDGE,"E22.1"),sQuery(id+"F13.wireOp",EDGE,"E22.2"),sQuery(id+"F13.wireOp",EDGE,"E22.3"),sQuery(id+"F13.wireOp",EDGE,"E22.4"),sQuery(id+"F13.wireOp",EDGE,"E22.5"),sQuery(id+"F13.wireOp",EDGE,"E22.6"),sQuery(id+"F13.wireOp",EDGE,"E22.7"),sQuery(id+"F13.wireOp",EDGE,"E22.8"),sQuery(id+"F13.wireOp",EDGE,"E22.9"),sQuery(id+"F13.wireOp",EDGE,"E23")])],"isStart":true});
            shell(context, id + "F33", {"entities" : qUnion([Q0]), "thickness" : 20 * mm});
        }
    });
